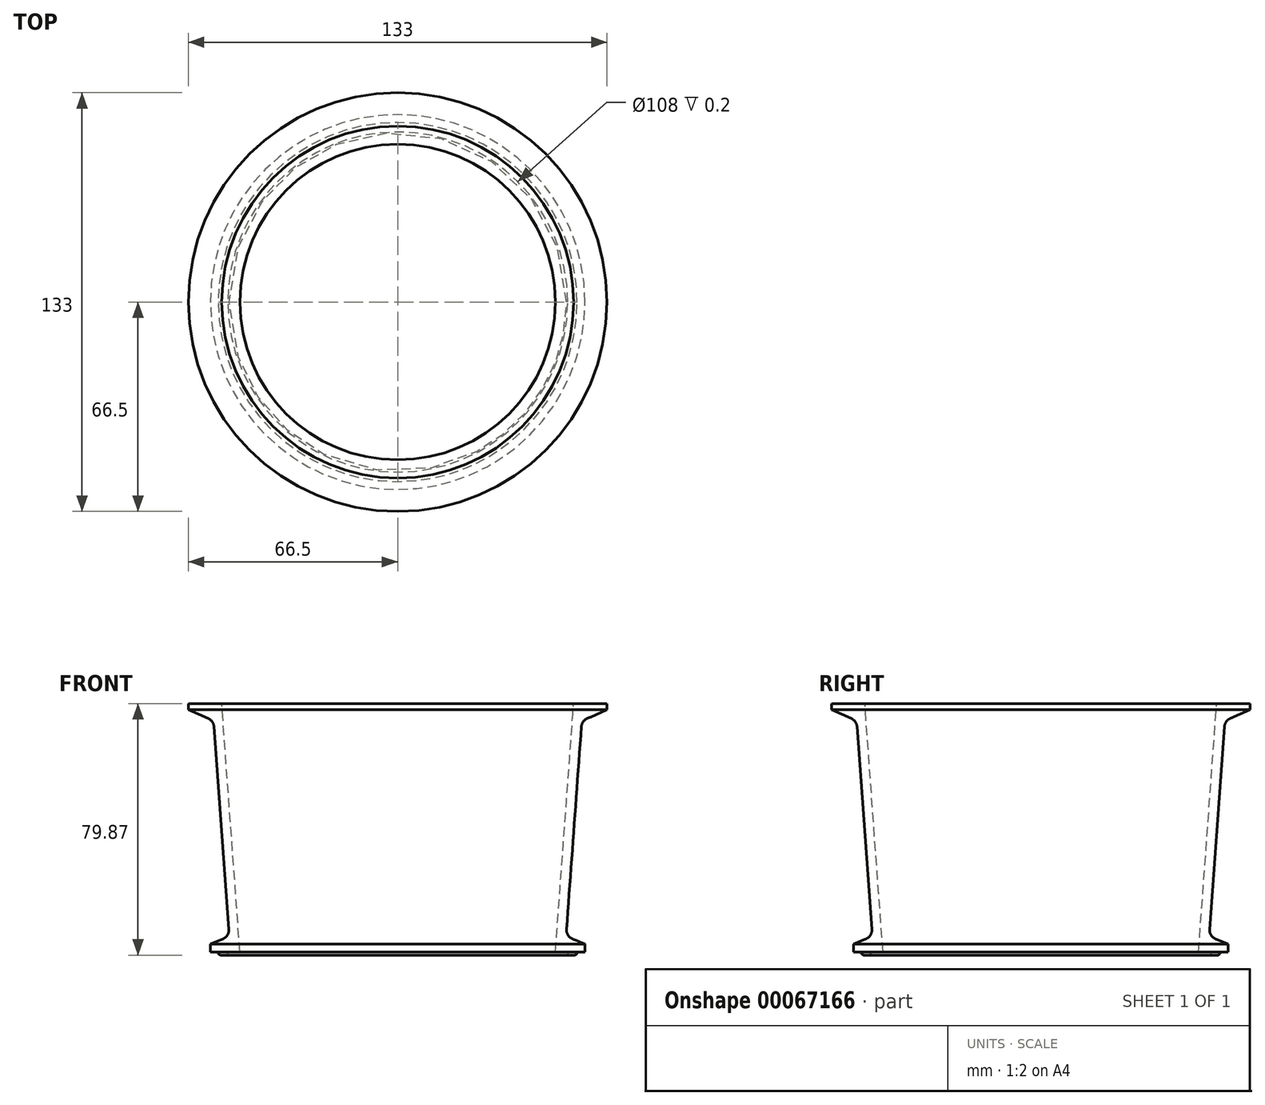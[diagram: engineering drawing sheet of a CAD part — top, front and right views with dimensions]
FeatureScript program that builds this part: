
annotation { "Feature Type Name" : "Feature", "Feature Type Description" : "" }
export const myFeature = defineFeature(function(context is Context, id is Id, definition is map)
    precondition{}
    {
        {
            var Q0;
            Q0=qCreatedBy(makeId("Front.planeOp"),FACE);
            var sketch = newSketch(context, id + "F0", { "sketchPlane" : qUnion([Q0])});
            skLineSegment(sketch, "E0", {"start": v(0, 59.01) * mm, "end": v(0, -79.47) * mm, "construction": true});
            skLineSegment(sketch, "E1", {"start": v(55.9, 40.85) * mm, "end": v(66.5, 40.85) * mm});
            skLineSegment(sketch, "E2", {"start": v(59.5, -38.02) * mm, "end": v(57, -38.02) * mm});
            skLineSegment(sketch, "E3.left", {"start": v(66.5, 40.85) * mm, "end": v(66.5, 38.85) * mm});
            skLineSegment(sketch, "E4.right", {"start": v(59.5, -38.02) * mm, "end": v(59.5, -35.52) * mm});
            skLineSegment(sketch, "E5", {"start": v(66.5, 38.85) * mm, "end": v(58.5, 35.35) * mm});
            skLineSegment(sketch, "E6", {"start": v(59.5, -35.52) * mm, "end": v(53.5, -33.02) * mm});
            skLineSegment(sketch, "E7", {"start": v(58.5, 35.35) * mm, "end": v(53.5, -33.02) * mm});
            skLineSegment(sketch, "E8.0", {"start": v(55.9, 40.85) * mm, "end": v(50.13, -38.02) * mm});
            skLineSegment(sketch, "E9.top", {"start": v(54, -39.02) * mm, "end": v(57, -39.02) * mm});
            skLineSegment(sketch, "E9.left", {"start": v(54, -39.02) * mm, "end": v(54, -38.02) * mm});
            skLineSegment(sketch, "E9.right", {"start": v(57, -39.02) * mm, "end": v(57, -38.02) * mm});
            skLineSegment(sketch, "E10", {"start": v(66.5, 38.85) * mm, "end": v(55.64, 38.85) * mm, "construction": true});
            skLineSegment(sketch, "E11.trimOffspring", {"start": v(54, -38.02) * mm, "end": v(50.13, -38.02) * mm});
            skSolve(sketch);
        }
        {
            var Q0;
            Q0=makeQuery(id+"F0.imprint","IMPRINT",FACE,{"disambiguationData":[TD([[makeQuery(id+"F0.imprint","IMPRINT",EDGE,{"derivedFrom":sQuery(id+"F0.wireOp",EDGE,"E1")}),-1.0]])]});
            var Q1;
            Q1=sQuery(id+"F0.wireOp",EDGE,"E0");
            revolve(context, id + "F1", {"entities" : qUnion([Q0]), "axis" : qUnion([Q1]), "revolveType" : RevolveType.FULL});
        }
        {
            var Q0;
            Q0=makeQuery(id+"F1.opRevolve","SWEPT_FACE",FACE,{"disambiguationData":[OSD([sQuery(id+"F0.wireOp",EDGE,"E9.top")])]});
            fillet(context, id + "F2", {"entities" : qUnion([Q0]), "radius" : .8 * mm, "tangentPropagation" : true, "allowEdgeOverflow" : false});
        }
        {
            var Q0;
            Q0=makeQuery(id+"F1.opRevolve","SWEPT_EDGE",EDGE,{"disambiguationData":[OSD([sQuery(id+"F0.wireOp",EDGE,"E5"),sQuery(id+"F0.wireOp",EDGE,"E7")])]});
            var Q1;
            Q1=makeQuery(id+"F1.opRevolve","SWEPT_EDGE",EDGE,{"disambiguationData":[OSD([sQuery(id+"F0.wireOp",EDGE,"E6"),sQuery(id+"F0.wireOp",EDGE,"E7")])]});
            fillet(context, id + "F3", {"entities" : qUnion([Q0, Q1]), "radius" : 3 * mm, "tangentPropagation" : true, "allowEdgeOverflow" : false});
        }
    });
